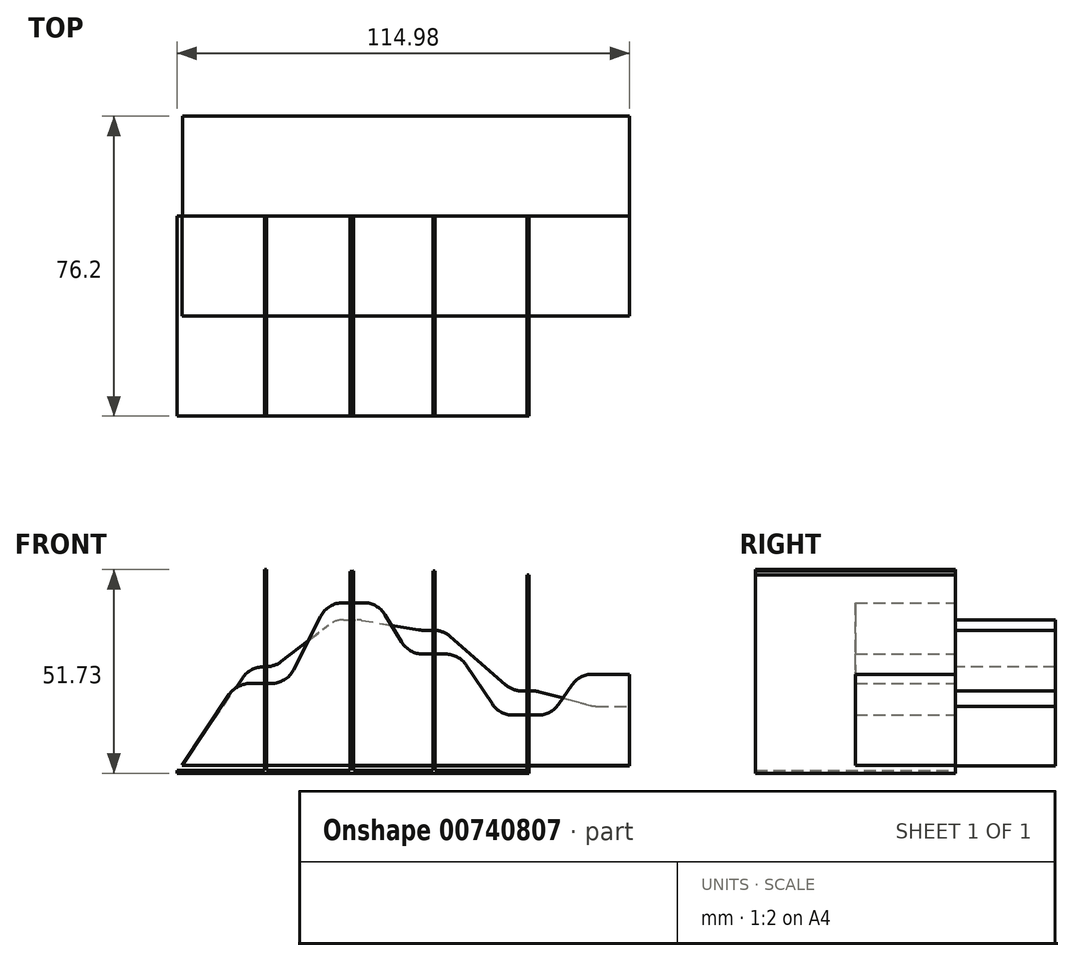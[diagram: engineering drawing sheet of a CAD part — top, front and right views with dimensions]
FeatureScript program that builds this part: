
annotation { "Feature Type Name" : "Feature", "Feature Type Description" : "" }
export const myFeature = defineFeature(function(context is Context, id is Id, definition is map)
    precondition{}
    {
        {
            var Q0;
            Q0=qCreatedBy(makeId("Front.planeOp"),FACE);
            var sketch = newSketch(context, id + "F0", { "sketchPlane" : qUnion([Q0])});
            skLineSegment(sketch, "E0", {"start": v(-42.8, -20.85) * mm, "end": v(-30.82, -2.84) * mm});
            skLineSegment(sketch, "E1", {"start": v(-25.53, 0) * mm, "end": v(-22.15, 0) * mm});
            skLineSegment(sketch, "E2", {"start": v(-22.15, 0) * mm, "end": v(-20.13, 0) * mm});
            skLineSegment(sketch, "E3", {"start": v(-14.47, 3.46) * mm, "end": v(-7.54, 17.06) * mm});
            skLineSegment(sketch, "E4", {"start": v(-1.88, 20.52) * mm, "end": v(3.34, 20.52) * mm});
            skLineSegment(sketch, "E5", {"start": v(8.76, 17.47) * mm, "end": v(13, 10.52) * mm});
            skLineSegment(sketch, "E6", {"start": v(18.42, 7.47) * mm, "end": v(24.13, 7.47) * mm});
            skLineSegment(sketch, "E7", {"start": v(29.4, 4.66) * mm, "end": v(36.04, -5.23) * mm});
            skLineSegment(sketch, "E8", {"start": v(41.31, -8.04) * mm, "end": v(47.64, -8.04) * mm});
            skLineSegment(sketch, "E9", {"start": v(52.87, -5.3) * mm, "end": v(56.27, -0.38) * mm});
            skLineSegment(sketch, "E10", {"start": v(61.5, 2.36) * mm, "end": v(70.84, 2.36) * mm});
            skArc(sketch, "E11.filletArc", {"start": v(61.5, 2.36) * mm, "mid": v(58.54, 1.64) * mm, "end": v(56.27, -0.38) * mm});
            skArc(sketch, "E12.filletArc", {"start": v(36.04, -5.23) * mm, "mid": v(38.32, -7.3) * mm, "end": v(41.31, -8.04) * mm});
            skArc(sketch, "E13.filletArc", {"start": v(47.64, -8.04) * mm, "mid": v(50.6, -7.31) * mm, "end": v(52.87, -5.3) * mm});
            skArc(sketch, "E14.filletArc", {"start": v(29.4, 4.66) * mm, "mid": v(27.12, 6.72) * mm, "end": v(24.13, 7.47) * mm});
            skArc(sketch, "E15.filletArc", {"start": v(13, 10.52) * mm, "mid": v(15.3, 8.29) * mm, "end": v(18.42, 7.47) * mm});
            skArc(sketch, "E16.filletArc", {"start": v(8.76, 17.47) * mm, "mid": v(6.45, 19.7) * mm, "end": v(3.34, 20.52) * mm});
            skArc(sketch, "E17.filletArc", {"start": v(-1.88, 20.52) * mm, "mid": v(-5.2, 19.59) * mm, "end": v(-7.54, 17.06) * mm});
            skArc(sketch, "E18.filletArc", {"start": v(-20.13, 0) * mm, "mid": v(-16.8, 0.94) * mm, "end": v(-14.47, 3.46) * mm});
            skArc(sketch, "E19.filletArc", {"start": v(-25.53, 0) * mm, "mid": v(-28.53, -0.75) * mm, "end": v(-30.82, -2.84) * mm});
            skLineSegment(sketch, "E20", {"start": v(-42.8, -20.85) * mm, "end": v(70.84, -20.85) * mm});
            skLineSegment(sketch, "E21", {"start": v(70.84, 2.36) * mm, "end": v(70.84, -20.85) * mm});
            skPoint(sketch, "E22.orphan", {"position": v(72.5, -20.85) * mm});
            skSolve(sketch);
        }
        {
            var Q0;
            Q0 = qSketchRegion(id + "F0", true);
            extrude(context, id + "F1", {"entities" : qUnion([Q0]), "depth" : 25.4 * mm, "offsetDistance" : 25.4 * mm});
        }
        {
            var Q0;
            Q0=qCreatedBy(makeId("Front.planeOp"),FACE);
            var sketch = newSketch(context, id + "F2", { "sketchPlane" : qUnion([Q0])});
            skLineSegment(sketch, "E23", {"start": v(70.88, -20.93) * mm, "end": v(-42.68, -20.85) * mm});
            skLineSegment(sketch, "E24", {"start": v(-42.68, -20.85) * mm, "end": v(-27.33, 1.5) * mm});
            skLineSegment(sketch, "E25", {"start": v(-22.1, 4.25) * mm, "end": v(-21.46, 4.25) * mm});
            skPoint(sketch, "E26.end.orphan", {"position": v(-22.76, 4.25) * mm});
            skLineSegment(sketch, "E27", {"start": v(-17.58, 5.57) * mm, "end": v(-5.6, 14.84) * mm});
            skLineSegment(sketch, "E28", {"start": v(-1.7, 16.17) * mm, "end": v(1.73, 16.17) * mm});
            skLineSegment(sketch, "E29", {"start": v(2.8, 16.08) * mm, "end": v(17.35, 13.61) * mm});
            skLineSegment(sketch, "E30", {"start": v(18.4, 13.52) * mm, "end": v(21.17, 13.52) * mm});
            skLineSegment(sketch, "E31", {"start": v(25.34, 11.96) * mm, "end": v(39.44, -0.33) * mm});
            skLineSegment(sketch, "E32", {"start": v(43.61, -1.9) * mm, "end": v(46.27, -1.9) * mm});
            skLineSegment(sketch, "E33", {"start": v(47.9, -2.1) * mm, "end": v(60.86, -5.56) * mm});
            skLineSegment(sketch, "E34", {"start": v(62.5, -5.77) * mm, "end": v(70.84, -5.77) * mm});
            skLineSegment(sketch, "E35", {"start": v(70.84, -5.77) * mm, "end": v(70.88, -20.93) * mm});
            skPoint(sketch, "E36.visualSharp", {"position": v(-3.88, 16.17) * mm});
            skArc(sketch, "E36.filletArc", {"start": v(-1.7, 16.17) * mm, "mid": v(-3.76, 15.83) * mm, "end": v(-5.6, 14.84) * mm});
            skPoint(sketch, "E37.visualSharp", {"position": v(2.27, 16.17) * mm});
            skArc(sketch, "E37.filletArc", {"start": v(2.8, 16.08) * mm, "mid": v(2.27, 16.15) * mm, "end": v(1.73, 16.17) * mm});
            skPoint(sketch, "E38.visualSharp", {"position": v(23.55, 13.52) * mm});
            skPoint(sketch, "E39.visualSharp", {"position": v(17.87, 13.52) * mm});
            skArc(sketch, "E39.filletArc", {"start": v(17.35, 13.61) * mm, "mid": v(17.88, 13.55) * mm, "end": v(18.4, 13.52) * mm});
            skPoint(sketch, "E40.visualSharp", {"position": v(47.1, -1.9) * mm});
            skArc(sketch, "E40.filletArc", {"start": v(47.9, -2.1) * mm, "mid": v(47.1, -1.95) * mm, "end": v(46.27, -1.9) * mm});
            skPoint(sketch, "E41.visualSharp", {"position": v(41.23, -1.9) * mm});
            skArc(sketch, "E41.filletArc", {"start": v(39.44, -0.33) * mm, "mid": v(41.39, -1.49) * mm, "end": v(43.61, -1.9) * mm});
            skPoint(sketch, "E42.visualSharp", {"position": v(61.66, -5.77) * mm});
            skArc(sketch, "E42.filletArc", {"start": v(60.86, -5.56) * mm, "mid": v(61.67, -5.72) * mm, "end": v(62.5, -5.77) * mm});
            skPoint(sketch, "E43.visualSharp", {"position": v(-25.44, 4.25) * mm});
            skArc(sketch, "E43.filletArc", {"start": v(-22.1, 4.25) * mm, "mid": v(-25.06, 3.51) * mm, "end": v(-27.33, 1.5) * mm});
            skPoint(sketch, "E44.visualSharp", {"position": v(-19.3, 4.25) * mm});
            skArc(sketch, "E44.filletArc", {"start": v(-21.46, 4.25) * mm, "mid": v(-19.4, 4.59) * mm, "end": v(-17.58, 5.57) * mm});
            skArc(sketch, "E45", {"start": v(25.34, 11.96) * mm, "mid": v(23.4, 13.12) * mm, "end": v(21.17, 13.52) * mm});
            skSolve(sketch);
        }
        {
            var Q0;
            Q0 = qSketchRegion(id + "F2", true);
            extrude(context, id + "F3", {"entities" : qUnion([Q0]), "oppositeDirection" : true, "depth" : 25.4 * mm, "offsetDistance" : 25.4 * mm});
        }
        {
            var Q0;
            Q0=qCreatedBy(makeId("Front.planeOp"),FACE);
            var sketch = newSketch(context, id + "F4", { "sketchPlane" : qUnion([Q0])});
            skLineSegment(sketch, "E46", {"start": v(-44.1, -22.8) * mm, "end": v(70.52, -22.8) * mm});
            skLineSegment(sketch, "E47", {"start": v(-44.1, -22.8) * mm, "end": v(-44.1, 28.55) * mm});
            skLineSegment(sketch, "E48", {"start": v(-21.88, -12.97) * mm, "end": v(-21.37, -12.97) * mm});
            skLineSegment(sketch, "E49", {"start": v(-0.13, -2.95) * mm, "end": v(0.73, -2.95) * mm});
            skLineSegment(sketch, "E50", {"start": v(-21.88, 7.55) * mm, "end": v(-21.37, 7.55) * mm});
            skLineSegment(sketch, "E51", {"start": v(-21.88, 16.16) * mm, "end": v(-21.37, 16.16) * mm});
            skLineSegment(sketch, "E52", {"start": v(-21.88, 22.87) * mm, "end": v(-21.37, 22.87) * mm});
            skLineSegment(sketch, "E53", {"start": v(-21.88, -22.8) * mm, "end": v(-21.88, 28.92) * mm});
            skLineSegment(sketch, "E54", {"start": v(-0.13, -22.8) * mm, "end": v(-0.13, 28.45) * mm});
            skLineSegment(sketch, "E55", {"start": v(20.96, -22.8) * mm, "end": v(20.96, 28.55) * mm});
            skLineSegment(sketch, "E56", {"start": v(44.8, -22.8) * mm, "end": v(44.8, 27.6) * mm});
            skLineSegment(sketch, "E57.0", {"start": v(-21.37, -22.8) * mm, "end": v(-21.37, 28.92) * mm});
            skLineSegment(sketch, "E58.0", {"start": v(0.73, -22.8) * mm, "end": v(0.73, 28.55) * mm});
            skLineSegment(sketch, "E59.0", {"start": v(21.47, -22.8) * mm, "end": v(21.47, 28.55) * mm});
            skLineSegment(sketch, "E60.0", {"start": v(45.3, -22.8) * mm, "end": v(45.3, 27.6) * mm});
            skLineSegment(sketch, "E61", {"start": v(-21.88, 28.92) * mm, "end": v(-21.37, 28.92) * mm});
            skLineSegment(sketch, "E62", {"start": v(-0.13, 28.45) * mm, "end": v(0.73, 28.55) * mm});
            skLineSegment(sketch, "E63", {"start": v(20.96, 28.55) * mm, "end": v(21.47, 28.55) * mm});
            skLineSegment(sketch, "E64", {"start": v(44.8, 27.6) * mm, "end": v(45.3, 27.6) * mm});
            skLineSegment(sketch, "E65.trimOffspring", {"start": v(-0.13, 22.87) * mm, "end": v(0.73, 22.87) * mm});
            skLineSegment(sketch, "E66.trimOffspring", {"start": v(-0.13, 16.16) * mm, "end": v(0.73, 16.16) * mm});
            skLineSegment(sketch, "E67.trimOffspring", {"start": v(20.96, 16.16) * mm, "end": v(21.47, 16.16) * mm});
            skLineSegment(sketch, "E68.trimOffspring", {"start": v(20.96, 22.87) * mm, "end": v(21.47, 22.87) * mm});
            skLineSegment(sketch, "E69.trimOffspring", {"start": v(44.8, 22.87) * mm, "end": v(45.3, 22.87) * mm});
            skLineSegment(sketch, "E70.trimOffspring", {"start": v(44.8, 16.16) * mm, "end": v(45.3, 16.16) * mm});
            skLineSegment(sketch, "E71.trimOffspring", {"start": v(44.8, 7.55) * mm, "end": v(45.3, 7.55) * mm});
            skLineSegment(sketch, "E72.trimOffspring", {"start": v(44.8, -2.95) * mm, "end": v(45.3, -2.95) * mm});
            skLineSegment(sketch, "E73.trimOffspring", {"start": v(44.8, -12.97) * mm, "end": v(45.3, -12.97) * mm});
            skLineSegment(sketch, "E74.trimOffspring", {"start": v(20.96, -12.97) * mm, "end": v(21.47, -12.97) * mm});
            skLineSegment(sketch, "E75.trimOffspring", {"start": v(20.96, -2.95) * mm, "end": v(21.47, -2.95) * mm});
            skLineSegment(sketch, "E76.trimOffspring", {"start": v(20.96, 7.55) * mm, "end": v(21.47, 7.55) * mm});
            skLineSegment(sketch, "E77.trimOffspring", {"start": v(-0.13, 7.55) * mm, "end": v(0.73, 7.55) * mm});
            skPoint(sketch, "E78.orphan", {"position": v(-44.1, -12.97) * mm});
            skLineSegment(sketch, "E79.trimOffspring", {"start": v(-0.13, -12.97) * mm, "end": v(0.73, -12.97) * mm});
            skLineSegment(sketch, "E80.0", {"start": v(-44.1, -22.05) * mm, "end": v(70.52, -22.05) * mm});
            skSolve(sketch);
        }
        {
            var Q0;
            Q0 = qSketchRegion(id + "F4", true);
            extrude(context, id + "F5", {"entities" : qUnion([Q0]), "depth" : 50.8 * mm, "offsetDistance" : 25.4 * mm});
        }
    });
